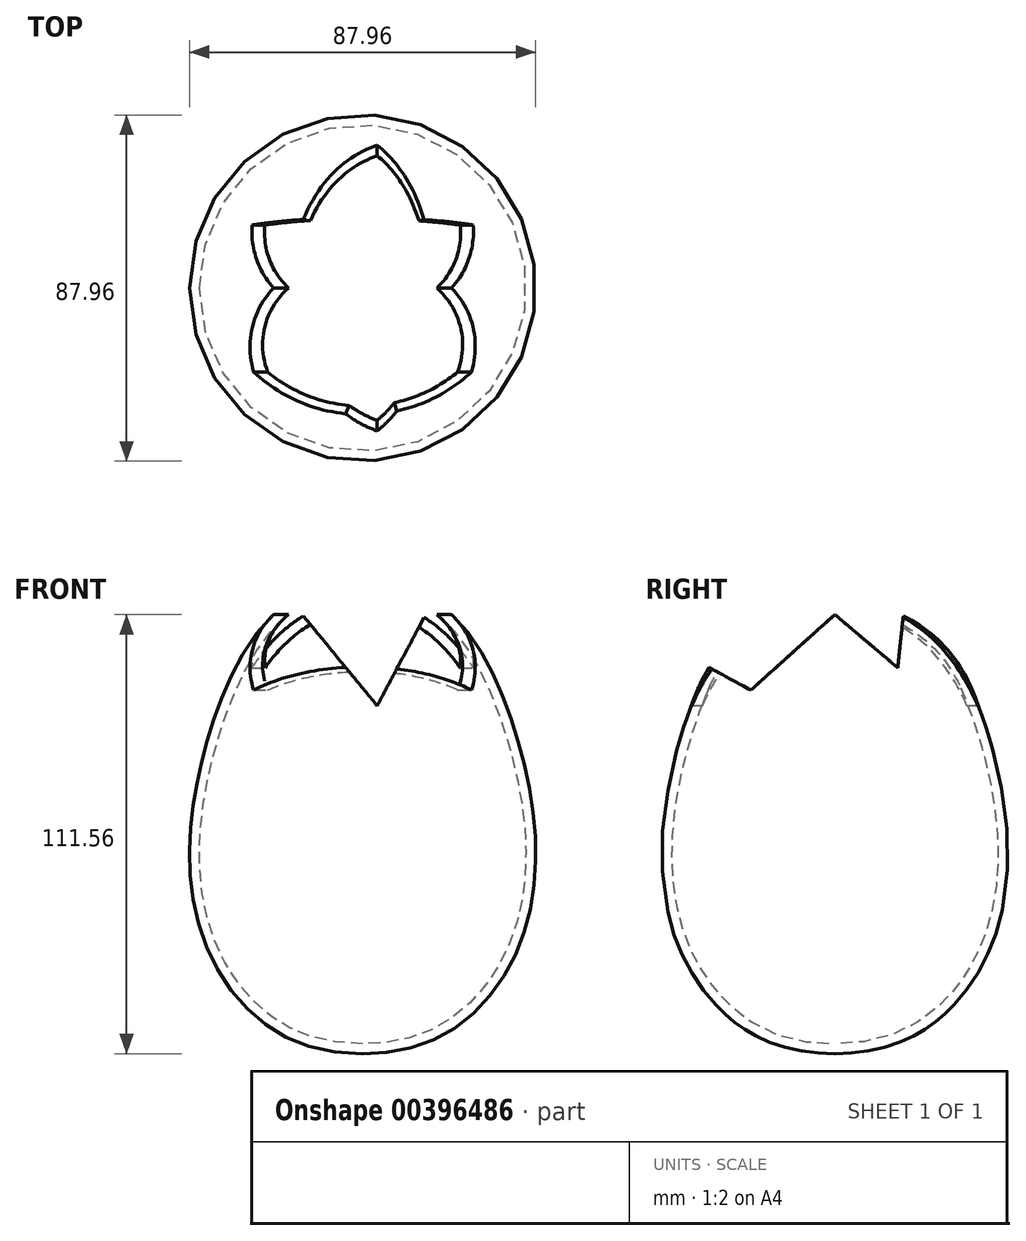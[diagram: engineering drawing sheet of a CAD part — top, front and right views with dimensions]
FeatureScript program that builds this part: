
annotation { "Feature Type Name" : "Feature", "Feature Type Description" : "" }
export const myFeature = defineFeature(function(context is Context, id is Id, definition is map)
    precondition{}
    {
        {
            var Q0;
            Q0=qCreatedBy(makeId("Front.planeOp"),FACE);
            var sketch = newSketch(context, id + "F0", { "sketchPlane" : qUnion([Q0])});
            skFitSpline(sketch, "E0", {"points": [v(0, 0) * mm, v(-24.72, 7.47) * mm, v(-39.46, 26.6) * mm, v(-43.98, 50.25) * mm, v(-41.65, 70.8) * mm, v(-35.97, 89.79) * mm, v(-23.34, 110.85) * mm, v(0, 121.76) * mm], "startDerivative": vector(-203.05, 0) * mm, "endDerivative": vector(172.53, 4.76) * mm});
            skLineSegment(sketch, "E1", {"start": v(0, 121.76) * mm, "end": v(0, 0) * mm});
            skSolve(sketch);
        }
        {
            var Q0;
            Q0 = qSketchRegion(id + "F0", true);
            var Q1;
            Q1=sQuery(id+"F0.wireOp",EDGE,"E1");
            revolve(context, id + "F1", {"entities" : qUnion([Q0]), "axis" : qUnion([Q1]), "revolveType" : RevolveType.FULL});
        }
        {
            var Q0;
            Q0=qCreatedBy(makeId("Right.planeOp"),FACE);
            var sketch = newSketch(context, id + "F2", { "sketchPlane" : qUnion([Q0])});
            skLineSegment(sketch, "E2", {"start": v(-53.06, 109.63) * mm, "end": v(-21.33, 92.37) * mm});
            skLineSegment(sketch, "E3", {"start": v(-21.33, 92.37) * mm, "end": v(0, 111.56) * mm});
            skLineSegment(sketch, "E4", {"start": v(0, 111.56) * mm, "end": v(16, 98.04) * mm});
            skLineSegment(sketch, "E5", {"start": v(16, 98.04) * mm, "end": v(19.2, 128.63) * mm});
            skLineSegment(sketch, "E6", {"start": v(-53.06, 109.63) * mm, "end": v(19.2, 128.63) * mm});
            skSolve(sketch);
        }
        {
            var Q0;
            Q0 = qSketchRegion(id + "F2", true);
            extrude(context, id + "F3", {"entities" : qUnion([Q0]), "operationType" : NewBodyOperationType.REMOVE, "endBound" : BoundingType.SYMMETRIC, "oppositeDirection" : true, "depth" : 90 * mm});
        }
        {
            var Q0;
            Q0=qCreatedBy(makeId("Front.planeOp"),FACE);
            var sketch = newSketch(context, id + "F4", { "sketchPlane" : qUnion([Q0])});
            skLineSegment(sketch, "E7", {"start": v(-23.35, 121.25) * mm, "end": v(3.7, 88.4) * mm});
            skLineSegment(sketch, "E8", {"start": v(3.7, 88.4) * mm, "end": v(20.89, 120.8) * mm});
            skLineSegment(sketch, "E9", {"start": v(-23.35, 121.25) * mm, "end": v(20.89, 120.8) * mm});
            skSolve(sketch);
        }
        {
            var Q0;
            Q0 = qSketchRegion(id + "F4", true);
            extrude(context, id + "F5", {"entities" : qUnion([Q0]), "operationType" : NewBodyOperationType.REMOVE, "endBound" : BoundingType.SYMMETRIC, "oppositeDirection" : true, "depth" : 100 * mm});
        }
        {
            var Q0;
            Q0=makeQuery(id+"F5.boolean.opBoolean","COPY",FACE,{"derivedFrom":makeQuery(id+"F5.opExtrude","SWEPT_FACE",FACE,{"disambiguationData":[OSD([sQuery(id+"F4.wireOp",EDGE,"E7")])]})});
            var Q1;
            Q1=makeQuery(id+"F5.boolean.opBoolean","COPY",FACE,{"derivedFrom":makeQuery(id+"F5.opExtrude","SWEPT_FACE",FACE,{"disambiguationData":[OSD([sQuery(id+"F4.wireOp",EDGE,"E8")])]})});
            var Q2;
            Q2=makeQuery(id+"F5.boolean.opBoolean","SPLIT",FACE,{"disambiguationData":[TD([makeQuery(id+"F5.opExtrude","SWEPT_FACE",FACE,{"disambiguationData":[OSD([sQuery(id+"F4.wireOp",EDGE,"E8")])]})])],"derivedFrom":makeQuery(id+"F3.boolean.opBoolean","COPY",FACE,{"derivedFrom":makeQuery(id+"F3.opExtrude","SWEPT_FACE",FACE,{"disambiguationData":[OSD([sQuery(id+"F2.wireOp",EDGE,"E3")])]})})});
            var Q3;
            Q3=makeQuery(id+"F5.boolean.opBoolean","SPLIT",FACE,{"disambiguationData":[TD([makeQuery(id+"F5.opExtrude","SWEPT_FACE",FACE,{"disambiguationData":[OSD([sQuery(id+"F4.wireOp",EDGE,"E8")])]})])],"derivedFrom":makeQuery(id+"F3.boolean.opBoolean","COPY",FACE,{"derivedFrom":makeQuery(id+"F3.opExtrude","SWEPT_FACE",FACE,{"disambiguationData":[OSD([sQuery(id+"F2.wireOp",EDGE,"E4")])]})})});
            var Q4;
            Q4=makeQuery(id+"F5.boolean.opBoolean","SPLIT",FACE,{"disambiguationData":[TD([makeQuery(id+"F5.opExtrude","SWEPT_FACE",FACE,{"disambiguationData":[OSD([sQuery(id+"F4.wireOp",EDGE,"E7")])]})])],"derivedFrom":makeQuery(id+"F3.boolean.opBoolean","COPY",FACE,{"derivedFrom":makeQuery(id+"F3.opExtrude","SWEPT_FACE",FACE,{"disambiguationData":[OSD([sQuery(id+"F2.wireOp",EDGE,"E4")])]})})});
            var Q5;
            Q5=makeQuery(id+"F5.boolean.opBoolean","SPLIT",FACE,{"disambiguationData":[TD([makeQuery(id+"F5.opExtrude","SWEPT_FACE",FACE,{"disambiguationData":[OSD([sQuery(id+"F4.wireOp",EDGE,"E7")])]})])],"derivedFrom":makeQuery(id+"F3.boolean.opBoolean","COPY",FACE,{"derivedFrom":makeQuery(id+"F3.opExtrude","SWEPT_FACE",FACE,{"disambiguationData":[OSD([sQuery(id+"F2.wireOp",EDGE,"E3")])]})})});
            var Q6;
            Q6=makeQuery(id+"F5.boolean.opBoolean","SPLIT",FACE,{"disambiguationData":[TD([makeQuery(id+"F5.opExtrude","SWEPT_FACE",FACE,{"disambiguationData":[OSD([sQuery(id+"F4.wireOp",EDGE,"E7")])]})])],"derivedFrom":makeQuery(id+"F3.boolean.opBoolean","COPY",FACE,{"derivedFrom":makeQuery(id+"F3.opExtrude","SWEPT_FACE",FACE,{"disambiguationData":[OSD([sQuery(id+"F2.wireOp",EDGE,"E5")])]})})});
            var Q7;
            Q7=makeQuery(id+"F5.boolean.opBoolean","SPLIT",FACE,{"disambiguationData":[TD([makeQuery(id+"F5.opExtrude","SWEPT_FACE",FACE,{"disambiguationData":[OSD([sQuery(id+"F4.wireOp",EDGE,"E8")])]})])],"derivedFrom":makeQuery(id+"F3.boolean.opBoolean","COPY",FACE,{"derivedFrom":makeQuery(id+"F3.opExtrude","SWEPT_FACE",FACE,{"disambiguationData":[OSD([sQuery(id+"F2.wireOp",EDGE,"E5")])]})})});
            var Q8;
            Q8=makeQuery(id+"F5.boolean.opBoolean","SPLIT",FACE,{"disambiguationData":[TD([makeQuery(id+"F5.opExtrude","SWEPT_FACE",FACE,{"disambiguationData":[OSD([sQuery(id+"F4.wireOp",EDGE,"E7")])]})])],"derivedFrom":makeQuery(id+"F3.boolean.opBoolean","COPY",FACE,{"derivedFrom":makeQuery(id+"F3.opExtrude","SWEPT_FACE",FACE,{"disambiguationData":[OSD([sQuery(id+"F2.wireOp",EDGE,"E2")])]})})});
            var Q9;
            Q9=makeQuery(id+"F5.boolean.opBoolean","SPLIT",FACE,{"disambiguationData":[TD([makeQuery(id+"F5.opExtrude","SWEPT_FACE",FACE,{"disambiguationData":[OSD([sQuery(id+"F4.wireOp",EDGE,"E8")])]})])],"derivedFrom":makeQuery(id+"F3.boolean.opBoolean","COPY",FACE,{"derivedFrom":makeQuery(id+"F3.opExtrude","SWEPT_FACE",FACE,{"disambiguationData":[OSD([sQuery(id+"F2.wireOp",EDGE,"E2")])]})})});
            shell(context, id + "F6", {"entities" : qUnion([Q0, Q1, Q2, Q3, Q4, Q5, Q6, Q7, Q8, Q9]), "thickness" : 2.5 * mm});
        }
        {
            var Q0;
            Q0=qCreatedBy(makeId("Front.planeOp"),FACE);
            cPlane(context, id + "F7", {"entities" : qUnion([Q0]), "cplaneType" : CPlaneType.OFFSET, "offset" : 42 * mm, "width" : 150 * mm, "height" : 150 * mm});
        }
    });
